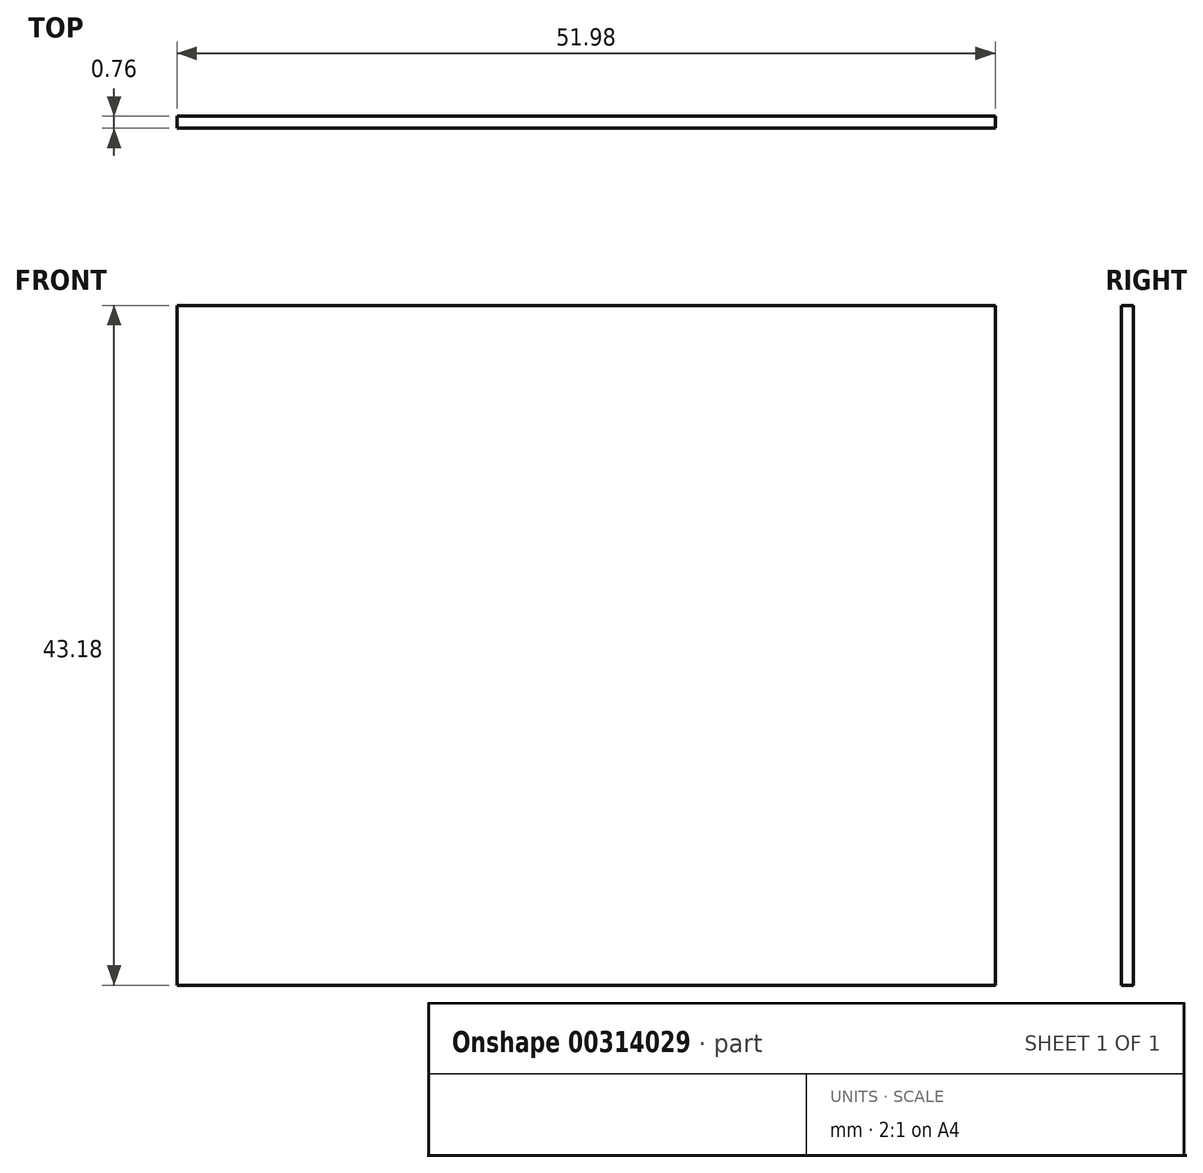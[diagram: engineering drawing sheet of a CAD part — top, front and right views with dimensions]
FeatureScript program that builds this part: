
annotation { "Feature Type Name" : "Feature", "Feature Type Description" : "" }
export const myFeature = defineFeature(function(context is Context, id is Id, definition is map)
    precondition{}
    {
        {
            var Q0;
            Q0=qCreatedBy(makeId("Front.planeOp"),FACE);
            var sketch = newSketch(context, id + "F0", { "sketchPlane" : qUnion([Q0])});
            skLineSegment(sketch, "E0.right", {"start": v(42.2, -23.71) * mm, "end": v(42.2, 19.47) * mm});
            skPoint(sketch, "E0.middle", {"position": v(0, 0) * mm});
            skLineSegment(sketch, "E1", {"start": v(42.2, 19.47) * mm, "end": v(-9.79, 19.47) * mm});
            skLineSegment(sketch, "E2", {"start": v(-9.79, 19.47) * mm, "end": v(-9.79, -23.71) * mm});
            skLineSegment(sketch, "E3", {"start": v(-9.79, -23.71) * mm, "end": v(42.2, -23.71) * mm});
            skSolve(sketch);
        }
        {
            var Q0;
            Q0 = qSketchRegion(id + "F0", true);
            extrude(context, id + "F1", {"entities" : qUnion([Q0]), "depth" : 0.76 * mm});
        }
    });
